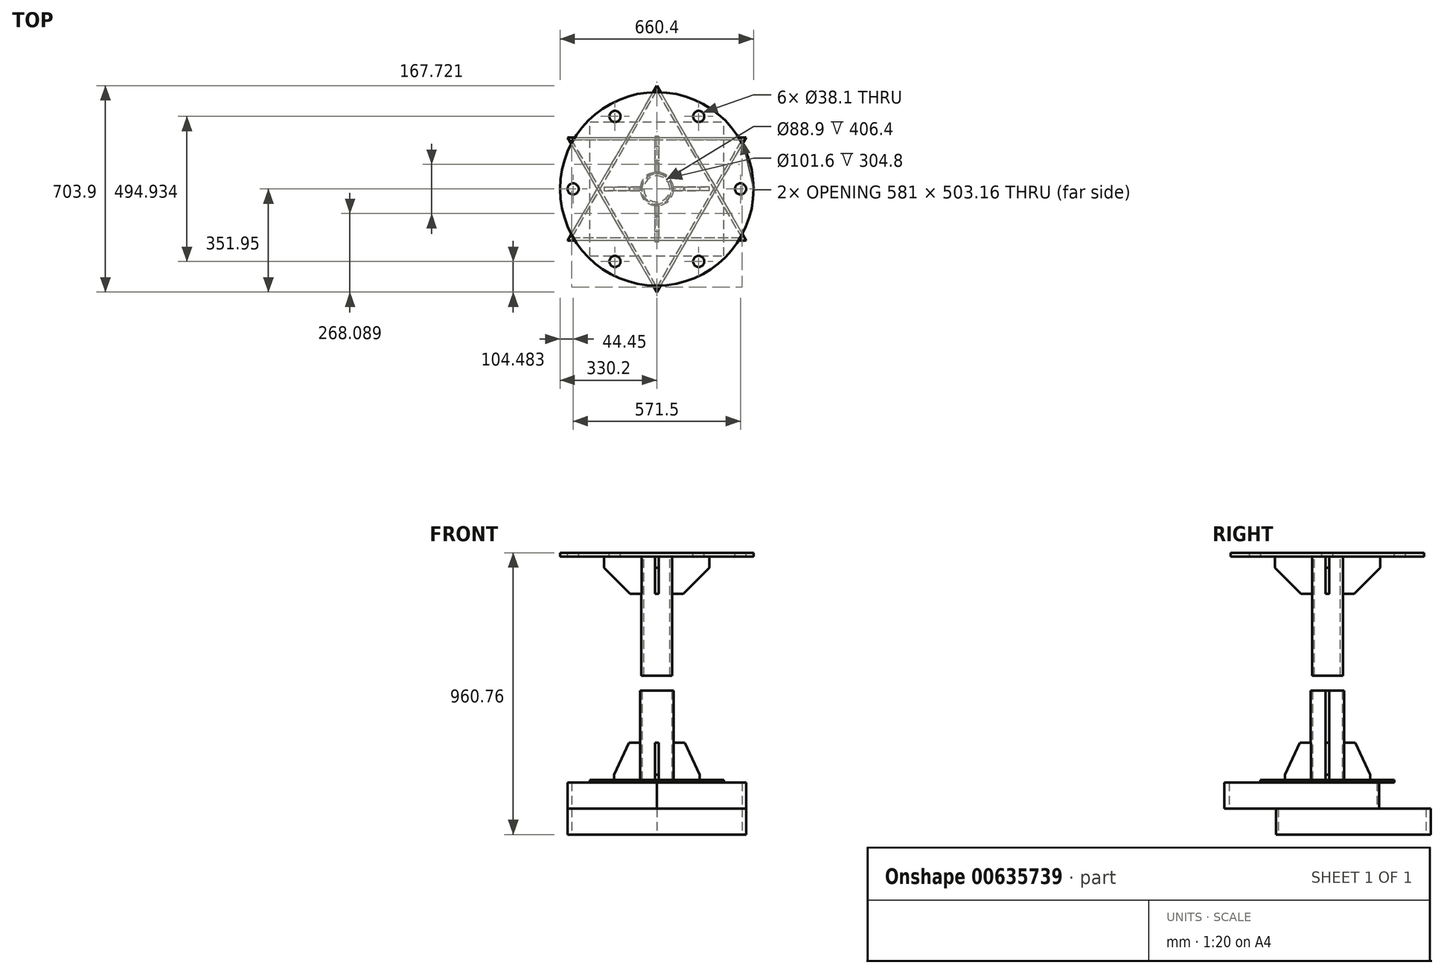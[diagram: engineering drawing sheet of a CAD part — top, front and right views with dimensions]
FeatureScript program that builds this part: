
annotation { "Feature Type Name" : "Feature", "Feature Type Description" : "" }
export const myFeature = defineFeature(function(context is Context, id is Id, definition is map)
    precondition{}
    {
        {
            var Q0;
            Q0=qCreatedBy(makeId("Top.planeOp"),FACE);
            var sketch = newSketch(context, id + "F0", { "sketchPlane" : qUnion([Q0])});
            skPoint(sketch, "E0.middle", {"position": v(0, 0) * mm});
            skCircle(sketch, "E1.cCircle", {"center": v(0, 0) * mm, "radius": 175.98 * mm, "construction": true});
            skLineSegment(sketch, "E1.0", {"start": v(304.8, -175.98) * mm, "end": v(-304.8, -175.98) * mm});
            skLineSegment(sketch, "E1.1", {"start": v(-304.8, -175.98) * mm, "end": v(0, 351.95) * mm});
            skLineSegment(sketch, "E1.2", {"start": v(0, 351.95) * mm, "end": v(304.8, -175.98) * mm});
            skPoint(sketch, "E1.0.midPoint", {"position": v(0, -175.98) * mm});
            skPoint(sketch, "E2.0.midPoint", {"position": v(-152.4, -87.99) * mm});
            skLineSegment(sketch, "E3.0", {"start": v(-290.5, -167.72) * mm, "end": v(0, 335.44) * mm});
            skLineSegment(sketch, "E3.1", {"start": v(290.5, -167.72) * mm, "end": v(-290.5, -167.72) * mm});
            skLineSegment(sketch, "E3.2", {"start": v(0, 335.44) * mm, "end": v(290.5, -167.72) * mm});
            skSolve(sketch);
        }
        {
            var Q0;
            Q0 = qSketchRegion(id + "F0", true);
            var Q1;
            Q1 = qConstructionFilter(qBodyType(qCreatedBy(id + "F0" ,EDGE), BodyType.WIRE), ConstructionObject.NO);
            extrude(context, id + "F1", {"entities" : qUnion([Q0]), "surfaceEntities" : qUnion([Q1]), "depth" : 88.9 * mm, "offsetDistance" : 25.4 * mm});
        }
        {
            var Q0;
            Q0=qCreatedBy(makeId("Top.planeOp"),FACE);
            cPlane(context, id + "F2", {"entities" : qUnion([Q0]), "cplaneType" : CPlaneType.OFFSET, "offset" : 88.9 * mm, "width" : 152.4 * mm, "height" : 152.4 * mm});
        }
        {
            var Q0;
            Q0=qCreatedBy(id+"F2.planeOp",FACE);
            var sketch = newSketch(context, id + "F3", { "sketchPlane" : qUnion([Q0])});
            skCircle(sketch, "E4.cCircle", {"center": v(0, 0) * mm, "radius": 175.98 * mm, "construction": true});
            skLineSegment(sketch, "E4.0", {"start": v(0, -351.95) * mm, "end": v(-304.8, 175.98) * mm});
            skLineSegment(sketch, "E4.1", {"start": v(-304.8, 175.98) * mm, "end": v(304.8, 175.98) * mm});
            skLineSegment(sketch, "E4.2", {"start": v(304.8, 175.98) * mm, "end": v(0, -351.95) * mm});
            skPoint(sketch, "E4.0.midPoint", {"position": v(-152.4, -87.99) * mm});
            skLineSegment(sketch, "E5.0", {"start": v(-290.5, 167.72) * mm, "end": v(290.5, 167.72) * mm});
            skLineSegment(sketch, "E5.1", {"start": v(0, -335.44) * mm, "end": v(-290.5, 167.72) * mm});
            skLineSegment(sketch, "E5.2", {"start": v(290.5, 167.72) * mm, "end": v(0, -335.44) * mm});
            skSolve(sketch);
        }
        {
            var Q0;
            Q0 = qSketchRegion(id + "F3", true);
            extrude(context, id + "F4", {"entities" : qUnion([Q0]), "depth" : 88.9 * mm, "offsetDistance" : 25.4 * mm});
        }
        {
            var Q0;
            Q0=makeQuery(id+"F4.opExtrude","CAP_FACE",FACE,{"disambiguationData":[OSD([sQuery(id+"F3.wireOp",EDGE,"E4.0"),sQuery(id+"F3.wireOp",EDGE,"E4.1"),sQuery(id+"F3.wireOp",EDGE,"E4.2"),sQuery(id+"F3.wireOp",EDGE,"E5.0"),sQuery(id+"F3.wireOp",EDGE,"E5.1"),sQuery(id+"F3.wireOp",EDGE,"E5.2")])],"isStart":false});
            var sketch = newSketch(context, id + "F5", { "sketchPlane" : qUnion([Q0])});
            skLineSegment(sketch, "E6.bottom", {"start": v(108.95, 167.72) * mm, "end": v(70.85, 167.72) * mm});
            skLineSegment(sketch, "E6.top", {"start": v(108.95, -162.48) * mm, "end": v(70.85, -162.48) * mm});
            skLineSegment(sketch, "E6.left", {"start": v(108.95, 167.72) * mm, "end": v(108.95, -162.48) * mm});
            skLineSegment(sketch, "E6.right", {"start": v(70.85, 167.72) * mm, "end": v(70.85, -162.48) * mm});
            skLineSegment(sketch, "E7.bottom", {"start": v(-99.89, 167.72) * mm, "end": v(-61.79, 167.72) * mm});
            skLineSegment(sketch, "E7.top", {"start": v(-99.89, -162.48) * mm, "end": v(-61.79, -162.48) * mm});
            skLineSegment(sketch, "E7.left", {"start": v(-99.89, 167.72) * mm, "end": v(-99.89, -162.48) * mm});
            skLineSegment(sketch, "E7.right", {"start": v(-61.79, 167.72) * mm, "end": v(-61.79, -162.48) * mm});
            skSolve(sketch);
        }
        {
            var Q0;
            Q0 = qSketchRegion(id + "F5", true);
            extrude(context, id + "F6", {"entities" : qUnion([Q0]), "depth" : 17.78 * mm, "offsetDistance" : 25.4 * mm});
        }
        {
            var Q0;
            Q0=makeQuery(id+"F4.opExtrude","CAP_FACE",FACE,{"disambiguationData":[OSD([sQuery(id+"F3.wireOp",EDGE,"E4.0"),sQuery(id+"F3.wireOp",EDGE,"E4.1"),sQuery(id+"F3.wireOp",EDGE,"E4.2"),sQuery(id+"F3.wireOp",EDGE,"E5.0"),sQuery(id+"F3.wireOp",EDGE,"E5.1"),sQuery(id+"F3.wireOp",EDGE,"E5.2")])],"isStart":false});
            var sketch = newSketch(context, id + "F7", { "sketchPlane" : qUnion([Q0])});
            skLineSegment(sketch, "E8.bottom", {"start": v(-228.6, -228.6) * mm, "end": v(228.6, -228.6) * mm});
            skLineSegment(sketch, "E8.top", {"start": v(-228.6, 228.6) * mm, "end": v(228.6, 228.6) * mm});
            skLineSegment(sketch, "E8.left", {"start": v(-228.6, -228.6) * mm, "end": v(-228.6, 228.6) * mm});
            skLineSegment(sketch, "E8.right", {"start": v(228.6, -228.6) * mm, "end": v(228.6, 228.6) * mm});
            skPoint(sketch, "E8.middle", {"position": v(0, 0) * mm});
            skSolve(sketch);
        }
        {
            var Q0;
            Q0 = qSketchRegion(id + "F7", true);
            extrude(context, id + "F8", {"entities" : qUnion([Q0]), "depth" : 8.25 * mm, "offsetDistance" : 25.4 * mm});
        }
        {
            var Q0;
            Q0=makeQuery(id+"F8.opExtrude","CAP_FACE",FACE,{"disambiguationData":[OSD([sQuery(id+"F7.wireOp",EDGE,"E8.bottom"),sQuery(id+"F7.wireOp",EDGE,"E8.top"),sQuery(id+"F7.wireOp",EDGE,"E8.left"),sQuery(id+"F7.wireOp",EDGE,"E8.right")])],"isStart":false});
            var sketch = newSketch(context, id + "F9", { "sketchPlane" : qUnion([Q0])});
            skCircle(sketch, "E9", {"center": v(0, 0) * mm, "radius": 50.8 * mm});
            skCircle(sketch, "E10.0", {"center": v(0, 0) * mm, "radius": 57.15 * mm});
            skLineSegment(sketch, "E11.bottom", {"start": v(56.8, -6.35) * mm, "end": v(145.7, -6.35) * mm});
            skLineSegment(sketch, "E11.top", {"start": v(56.8, 6.35) * mm, "end": v(145.7, 6.35) * mm});
            skLineSegment(sketch, "E11.left", {"start": v(56.8, -6.35) * mm, "end": v(56.8, 6.35) * mm});
            skLineSegment(sketch, "E11.right", {"start": v(145.7, -6.35) * mm, "end": v(145.7, 6.35) * mm});
            skPoint(sketch, "E11.middle", {"position": v(101.25, 0) * mm});
            skLineSegment(sketch, "E12.1.0", {"start": v(-6.35, 56.8) * mm, "end": v(-6.35, 145.7) * mm});
            skLineSegment(sketch, "E12.1.1", {"start": v(6.35, 56.8) * mm, "end": v(6.35, 145.7) * mm});
            skLineSegment(sketch, "E12.1.2", {"start": v(6.35, 145.7) * mm, "end": v(-6.35, 145.7) * mm});
            skLineSegment(sketch, "E12.2.0", {"start": v(-56.8, -6.35) * mm, "end": v(-145.7, -6.35) * mm});
            skLineSegment(sketch, "E12.2.1", {"start": v(-56.8, 6.35) * mm, "end": v(-145.7, 6.35) * mm});
            skLineSegment(sketch, "E12.2.2", {"start": v(-145.7, 6.35) * mm, "end": v(-145.7, -6.35) * mm});
            skLineSegment(sketch, "E13.1.3.0", {"start": v(6.35, -56.8) * mm, "end": v(6.35, -145.7) * mm});
            skLineSegment(sketch, "E13.3.3.0", {"start": v(-6.35, -56.8) * mm, "end": v(-6.35, -145.7) * mm});
            skLineSegment(sketch, "E13.6.3.0", {"start": v(-6.35, -145.7) * mm, "end": v(6.35, -145.7) * mm});
            skSolve(sketch);
        }
        {
            var Q0;
            Q0=makeQuery(id+"F9.imprint","IMPRINT",FACE,{"disambiguationData":[TD([[makeQuery(id+"F9.imprint","IMPRINT",EDGE,{"derivedFrom":sQuery(id+"F9.wireOp",EDGE,"E9")}),-1.0]])]});
            extrude(context, id + "F10", {"entities" : qUnion([Q0]), "depth" : 304.8 * mm, "offsetDistance" : 25.4 * mm});
        }
        {
            var Q0;
            {var subQ0=sQuery(id+"F9.wireOp",EDGE,"E12.2.0");Q0=makeQuery(id+"F9.imprint","IMPRINT",FACE,{"disambiguationData":[TD([[makeQuery(id+"F9.imprint","IMPRINT",EDGE,{"derivedFrom":subQ0}),-1.0]])]});}
            var Q1;
            {var subQ0=sQuery(id+"F9.wireOp",EDGE,"E13.1.3.0");Q1=makeQuery(id+"F9.imprint","IMPRINT",FACE,{"disambiguationData":[TD([[makeQuery(id+"F9.imprint","IMPRINT",EDGE,{"derivedFrom":subQ0}),-1.0]])]});}
            var Q2;
            {var subQ0=sQuery(id+"F9.wireOp",EDGE,"E12.1.0");Q2=makeQuery(id+"F9.imprint","IMPRINT",FACE,{"disambiguationData":[TD([[makeQuery(id+"F9.imprint","IMPRINT",EDGE,{"derivedFrom":subQ0}),-1.0]])]});}
            var Q3;
            {var subQ1=sQuery(id+"F9.wireOp",EDGE,"E11.bottom");Q3=makeQuery(id+"F9.imprint","IMPRINT",FACE,{"disambiguationData":[TD([[makeQuery(id+"F9.imprint","IMPRINT",EDGE,{"derivedFrom":subQ1}),1.0]])]});}
            extrude(context, id + "F11", {"entities" : qUnion([Q0, Q1, Q2, Q3]), "depth" : 127 * mm, "offsetDistance" : 25.4 * mm});
        }
        {
            var Q0;
            Q0=makeQuery(id+"F11.opExtrude","CAP_EDGE",EDGE,{"disambiguationData":[OSD([sQuery(id+"F9.wireOp",EDGE,"E11.right")])],"isStart":false});
            var Q1;
            Q1=makeQuery(id+"F11.opExtrude","CAP_EDGE",EDGE,{"disambiguationData":[OSD([sQuery(id+"F9.wireOp",EDGE,"E13.6.3.0")])],"isStart":false});
            var Q2;
            Q2=makeQuery(id+"F11.opExtrude","CAP_EDGE",EDGE,{"disambiguationData":[OSD([sQuery(id+"F9.wireOp",EDGE,"E12.2.2")])],"isStart":false});
            var Q3;
            Q3=makeQuery(id+"F11.opExtrude","CAP_EDGE",EDGE,{"disambiguationData":[OSD([sQuery(id+"F9.wireOp",EDGE,"E12.1.2")])],"isStart":false});
            chamfer(context, id + "F12", {"entities" : qUnion([Q0, Q1, Q2, Q3]), "chamferType" : ChamferType.OFFSET_ANGLE, "width" : 50.8 * mm, "oppositeDirection" : false, "angle" : 65 * degree, "tangentPropagation" : true});
        }
        {
            var Q0;
            Q0=makeQuery(id+"F10.opExtrude","CAP_FACE",FACE,{"disambiguationData":[OSD([sQuery(id+"F9.wireOp",EDGE,"E9"),sQuery(id+"F9.wireOp",EDGE,"E10.0"),sQuery(id+"F9.wireOp",EDGE,"E11.left")])],"isStart":false});
            cPlane(context, id + "F13", {"entities" : qUnion([Q0]), "cplaneType" : CPlaneType.OFFSET, "offset" : 457.2 * mm, "width" : 152.4 * mm, "height" : 152.4 * mm});
        }
        {
            var Q0;
            Q0=qCreatedBy(id+"F13.planeOp",FACE);
            var sketch = newSketch(context, id + "F14", { "sketchPlane" : qUnion([Q0])});
            skCircle(sketch, "E14", {"center": v(0, 0) * mm, "radius": 44.45 * mm});
            skCircle(sketch, "E15.0", {"center": v(0, 0) * mm, "radius": 52.7 * mm});
            skCircle(sketch, "E16", {"center": v(0, 0) * mm, "radius": 330.2 * mm});
            skLineSegment(sketch, "E17.bottom", {"start": v(-179.7, -6.3) * mm, "end": v(-52.33, -6.3) * mm});
            skLineSegment(sketch, "E17.top", {"start": v(-179.7, 6.4) * mm, "end": v(-52.31, 6.4) * mm});
            skLineSegment(sketch, "E17.left", {"start": v(-179.7, -6.3) * mm, "end": v(-179.7, 6.4) * mm});
            skPoint(sketch, "E17.middle", {"position": v(-80.74, 0) * mm});
            skLineSegment(sketch, "E18.1.0", {"start": v(6.4, 179.7) * mm, "end": v(6.4, 52.31) * mm});
            skLineSegment(sketch, "E18.1.1", {"start": v(-6.3, 179.7) * mm, "end": v(-6.3, 52.33) * mm});
            skLineSegment(sketch, "E18.1.2", {"start": v(-6.3, 179.7) * mm, "end": v(6.4, 179.7) * mm});
            skLineSegment(sketch, "E18.2.0", {"start": v(179.7, -6.4) * mm, "end": v(52.31, -6.4) * mm});
            skLineSegment(sketch, "E18.2.1", {"start": v(179.7, 6.3) * mm, "end": v(52.33, 6.3) * mm});
            skLineSegment(sketch, "E18.2.2", {"start": v(179.7, 6.3) * mm, "end": v(179.7, -6.4) * mm});
            skLineSegment(sketch, "E18.3.0", {"start": v(-6.4, -179.7) * mm, "end": v(-6.4, -52.31) * mm});
            skLineSegment(sketch, "E18.3.1", {"start": v(6.3, -179.7) * mm, "end": v(6.3, -52.33) * mm});
            skLineSegment(sketch, "E18.3.2", {"start": v(6.3, -179.7) * mm, "end": v(-6.4, -179.7) * mm});
            skLineSegment(sketch, "E18.anchor1", {"start": v(0, 0) * mm, "end": v(-179.7, 6.4) * mm, "construction": true});
            skLineSegment(sketch, "E18.anchor2", {"start": v(0, 0) * mm, "end": v(-6.4, -179.7) * mm, "construction": true});
            skSolve(sketch);
        }
        {
            var Q0;
            {var subQ0=sQuery(id+"F14.wireOp",EDGE,"E18.1.0");Q0=makeQuery(id+"F14.imprint","IMPRINT",FACE,{"disambiguationData":[TD([[makeQuery(id+"F14.imprint","IMPRINT",EDGE,{"derivedFrom":subQ0}),-1.0]])]});}
            var Q1;
            {var subQ0=sQuery(id+"F14.wireOp",EDGE,"E17.bottom");Q1=makeQuery(id+"F14.imprint","IMPRINT",FACE,{"disambiguationData":[TD([[makeQuery(id+"F14.imprint","IMPRINT",EDGE,{"derivedFrom":subQ0}),1.0]])]});}
            var Q2;
            {var subQ0=sQuery(id+"F14.wireOp",EDGE,"E18.3.0");Q2=makeQuery(id+"F14.imprint","IMPRINT",FACE,{"disambiguationData":[TD([[makeQuery(id+"F14.imprint","IMPRINT",EDGE,{"derivedFrom":subQ0}),-1.0]])]});}
            var Q3;
            {var subQ0=sQuery(id+"F14.wireOp",EDGE,"E18.2.0");Q3=makeQuery(id+"F14.imprint","IMPRINT",FACE,{"disambiguationData":[TD([[makeQuery(id+"F14.imprint","IMPRINT",EDGE,{"derivedFrom":subQ0}),-1.0]])]});}
            extrude(context, id + "F15", {"entities" : qUnion([Q0, Q1, Q2, Q3]), "oppositeDirection" : true, "depth" : 127 * mm, "offsetDistance" : 25.4 * mm});
        }
        {
            var Q0;
            Q0=makeQuery(id+"F14.imprint","IMPRINT",FACE,{"disambiguationData":[TD([[makeQuery(id+"F14.imprint","IMPRINT",EDGE,{"derivedFrom":sQuery(id+"F14.wireOp",EDGE,"E14")}),-1.0]])]});
            extrude(context, id + "F16", {"entities" : qUnion([Q0]), "oppositeDirection" : true, "depth" : 406.4 * mm, "offsetDistance" : 25.4 * mm});
        }
        {
            var Q0;
            Q0=makeQuery(id+"F14.imprint","IMPRINT",FACE,{"disambiguationData":[TD([[makeQuery(id+"F14.imprint","IMPRINT",EDGE,{"derivedFrom":sQuery(id+"F14.wireOp",EDGE,"E16")}),1.0]])]});
            var Q1;
            Q1=makeQuery(id+"F14.imprint","IMPRINT",FACE,{"disambiguationData":[TD([[makeQuery(id+"F14.imprint","IMPRINT",EDGE,{"derivedFrom":sQuery(id+"F14.wireOp",EDGE,"E14")}),-1.0]])]});
            var Q2;
            {var subQ0=sQuery(id+"F14.wireOp",EDGE,"E18.3.0");Q2=makeQuery(id+"F14.imprint","IMPRINT",FACE,{"disambiguationData":[TD([[makeQuery(id+"F14.imprint","IMPRINT",EDGE,{"derivedFrom":subQ0}),-1.0]])]});}
            var Q3;
            {var subQ0=sQuery(id+"F14.wireOp",EDGE,"E18.2.0");Q3=makeQuery(id+"F14.imprint","IMPRINT",FACE,{"disambiguationData":[TD([[makeQuery(id+"F14.imprint","IMPRINT",EDGE,{"derivedFrom":subQ0}),-1.0]])]});}
            var Q4;
            {var subQ0=sQuery(id+"F14.wireOp",EDGE,"E17.bottom");Q4=makeQuery(id+"F14.imprint","IMPRINT",FACE,{"disambiguationData":[TD([[makeQuery(id+"F14.imprint","IMPRINT",EDGE,{"derivedFrom":subQ0}),1.0]])]});}
            var Q5;
            {var subQ0=sQuery(id+"F14.wireOp",EDGE,"E18.1.0");Q5=makeQuery(id+"F14.imprint","IMPRINT",FACE,{"disambiguationData":[TD([[makeQuery(id+"F14.imprint","IMPRINT",EDGE,{"derivedFrom":subQ0}),-1.0]])]});}
            var Q6;
            Q6=makeQuery(id+"F14.imprint","IMPRINT",FACE,{"disambiguationData":[TD([[makeQuery(id+"F14.imprint","IMPRINT",EDGE,{"derivedFrom":sQuery(id+"F14.wireOp",EDGE,"E14")}),1.0]])]});
            extrude(context, id + "F17", {"entities" : qUnion([Q0, Q1, Q2, Q3, Q4, Q5, Q6]), "depth" : 12.7 * mm, "offsetDistance" : 25.4 * mm});
        }
        {
            var Q0;
            Q0=makeQuery(id+"F15.opExtrude","CAP_EDGE",EDGE,{"disambiguationData":[OSD([sQuery(id+"F14.wireOp",EDGE,"E18.1.2")])],"isStart":false});
            var Q1;
            Q1=makeQuery(id+"F15.opExtrude","CAP_EDGE",EDGE,{"disambiguationData":[OSD([sQuery(id+"F14.wireOp",EDGE,"E18.2.2")])],"isStart":false});
            var Q2;
            Q2=makeQuery(id+"F15.opExtrude","CAP_EDGE",EDGE,{"disambiguationData":[OSD([sQuery(id+"F14.wireOp",EDGE,"E17.left")])],"isStart":false});
            var Q3;
            Q3=makeQuery(id+"F15.opExtrude","CAP_EDGE",EDGE,{"disambiguationData":[OSD([sQuery(id+"F14.wireOp",EDGE,"E18.3.2")])],"isStart":false});
            chamfer(context, id + "F18", {"entities" : qUnion([Q0, Q1, Q2, Q3]), "width" : 88.9 * mm, "tangentPropagation" : true});
        }
        {
            var Q0;
            Q0=makeQuery(id+"F6.opExtrude","SWEPT_BODY",BODY,{"disambiguationData":[OSD([sQuery(id+"F5.wireOp",EDGE,"E6.bottom"),sQuery(id+"F5.wireOp",EDGE,"E6.top"),sQuery(id+"F5.wireOp",EDGE,"E6.left"),sQuery(id+"F5.wireOp",EDGE,"E6.right")])]});
            deleteBodies(context, id + "F19", {"entities" : qUnion([Q0])});
        }
        {
            var Q0;
            Q0=makeQuery(id+"F6.opExtrude","SWEPT_BODY",BODY,{"disambiguationData":[OSD([sQuery(id+"F5.wireOp",EDGE,"E7.bottom"),sQuery(id+"F5.wireOp",EDGE,"E7.top"),sQuery(id+"F5.wireOp",EDGE,"E7.left"),sQuery(id+"F5.wireOp",EDGE,"E7.right")])]});
            deleteBodies(context, id + "F20", {"entities" : qUnion([Q0])});
        }
        {
            var Q0;
            Q0=makeQuery(id+"F17.opExtrude","CAP_FACE",FACE,{"disambiguationData":[OSD([sQuery(id+"F14.wireOp",EDGE,"E16")])],"isStart":false});
            var sketch = newSketch(context, id + "F21", { "sketchPlane" : qUnion([Q0])});
            skCircle(sketch, "E19", {"center": v(-285.75, 0) * mm, "radius": 19.05 * mm});
            skCircle(sketch, "E20.1.0", {"center": v(-142.88, -247.47) * mm, "radius": 19.05 * mm});
            skCircle(sketch, "E20.2.0", {"center": v(142.87, -247.47) * mm, "radius": 19.05 * mm});
            skCircle(sketch, "E20.3.0", {"center": v(285.75, 0) * mm, "radius": 19.05 * mm});
            skCircle(sketch, "E20.4.0", {"center": v(142.88, 247.47) * mm, "radius": 19.05 * mm});
            skCircle(sketch, "E20.5.0", {"center": v(-142.88, 247.47) * mm, "radius": 19.05 * mm});
            skPoint(sketch, "E20.center", {"position": v(0, 0) * mm});
            skSolve(sketch);
        }
        {
            var Q0;
            Q0=makeQuery(id+"F21.imprint","IMPRINT",FACE,{"disambiguationData":[TD([[makeQuery(id+"F21.imprint","IMPRINT",EDGE,{"derivedFrom":sQuery(id+"F21.wireOp",EDGE,"E19")}),1.0]])]});
            var Q1;
            Q1=makeQuery(id+"F21.imprint","IMPRINT",FACE,{"disambiguationData":[TD([[makeQuery(id+"F21.imprint","IMPRINT",EDGE,{"derivedFrom":sQuery(id+"F21.wireOp",EDGE,"E20.5.0")}),1.0]])]});
            var Q2;
            Q2=makeQuery(id+"F21.imprint","IMPRINT",FACE,{"disambiguationData":[TD([[makeQuery(id+"F21.imprint","IMPRINT",EDGE,{"derivedFrom":sQuery(id+"F21.wireOp",EDGE,"E20.4.0")}),1.0]])]});
            var Q3;
            Q3=makeQuery(id+"F21.imprint","IMPRINT",FACE,{"disambiguationData":[TD([[makeQuery(id+"F21.imprint","IMPRINT",EDGE,{"derivedFrom":sQuery(id+"F21.wireOp",EDGE,"E20.3.0")}),1.0]])]});
            var Q4;
            Q4=makeQuery(id+"F21.imprint","IMPRINT",FACE,{"disambiguationData":[TD([[makeQuery(id+"F21.imprint","IMPRINT",EDGE,{"derivedFrom":sQuery(id+"F21.wireOp",EDGE,"E20.2.0")}),1.0]])]});
            var Q5;
            Q5=makeQuery(id+"F21.imprint","IMPRINT",FACE,{"disambiguationData":[TD([[makeQuery(id+"F21.imprint","IMPRINT",EDGE,{"derivedFrom":sQuery(id+"F21.wireOp",EDGE,"E20.1.0")}),1.0]])]});
            extrude(context, id + "F22", {"entities" : qUnion([Q0, Q1, Q2, Q3, Q4, Q5]), "operationType" : NewBodyOperationType.REMOVE, "endBound" : BoundingType.THROUGH_ALL, "oppositeDirection" : true, "depth" : 25.4 * mm, "offsetDistance" : 25.4 * mm});
        }
    });
